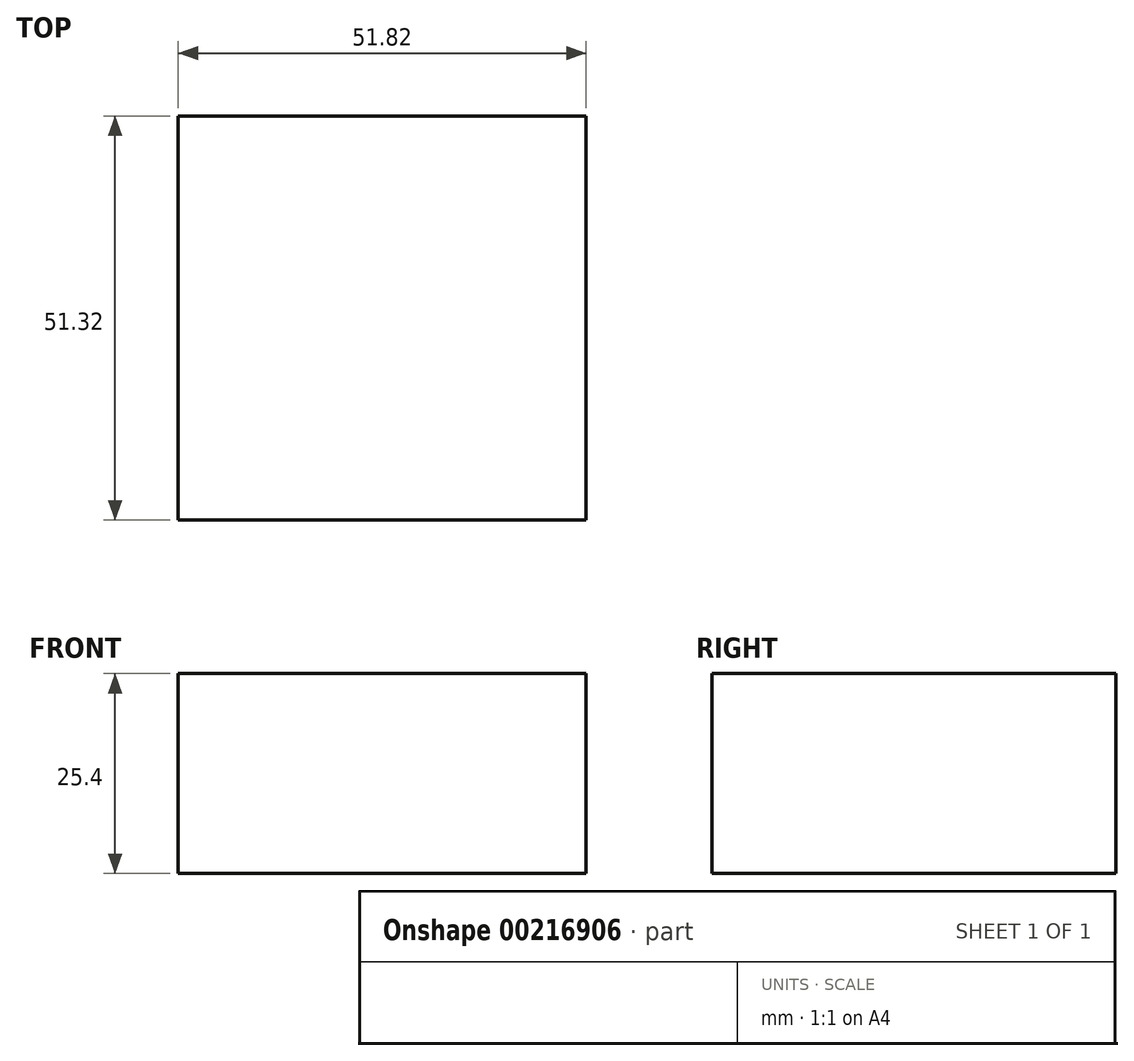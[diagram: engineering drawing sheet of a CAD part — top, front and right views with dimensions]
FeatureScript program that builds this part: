
annotation { "Feature Type Name" : "Feature", "Feature Type Description" : "" }
export const myFeature = defineFeature(function(context is Context, id is Id, definition is map)
    precondition{}
    {
        {
            var Q0;
            Q0=qCreatedBy(makeId("Top.planeOp"),FACE);
            var sketch = newSketch(context, id + "F0", { "sketchPlane" : qUnion([Q0])});
            skLineSegment(sketch, "E0", {"start": v(0, 0) * mm, "end": v(0, 51.32) * mm});
            skLineSegment(sketch, "E1", {"start": v(0, 51.32) * mm, "end": v(51.82, 51.32) * mm});
            skLineSegment(sketch, "E2", {"start": v(51.82, 51.32) * mm, "end": v(51.82, 0) * mm});
            skLineSegment(sketch, "E3", {"start": v(51.82, 0) * mm, "end": v(0, 0) * mm});
            skLineSegment(sketch, "E4.bottom", {"start": v(-45.17, 23.35) * mm, "end": v(-10.5, 23.35) * mm});
            skLineSegment(sketch, "E4.top", {"start": v(-45.17, -12.67) * mm, "end": v(-10.5, -12.67) * mm});
            skLineSegment(sketch, "E4.left", {"start": v(-45.17, 23.35) * mm, "end": v(-45.17, -12.67) * mm});
            skLineSegment(sketch, "E4.right", {"start": v(-10.5, 23.35) * mm, "end": v(-10.5, -12.67) * mm});
            skLineSegment(sketch, "E5.bottom", {"start": v(-10.5, -12.67) * mm, "end": v(12.96, -12.67) * mm});
            skLineSegment(sketch, "E5.top", {"start": v(-10.5, -59.16) * mm, "end": v(12.96, -59.16) * mm});
            skLineSegment(sketch, "E5.left", {"start": v(-10.5, -12.67) * mm, "end": v(-10.5, -59.16) * mm});
            skLineSegment(sketch, "E5.right", {"start": v(12.96, -12.67) * mm, "end": v(12.96, -59.16) * mm});
            skLineSegment(sketch, "E6.bottom", {"start": v(-10.5, 23.35) * mm, "end": v(-42.75, 23.35) * mm});
            skLineSegment(sketch, "E6.top", {"start": v(-10.5, 56.42) * mm, "end": v(-42.75, 56.42) * mm});
            skLineSegment(sketch, "E6.left", {"start": v(-10.5, 23.35) * mm, "end": v(-10.5, 56.42) * mm});
            skLineSegment(sketch, "E6.right", {"start": v(-42.75, 23.35) * mm, "end": v(-42.75, 56.42) * mm});
            skLineSegment(sketch, "E7.bottom", {"start": v(-45.17, -12.67) * mm, "end": v(-59.37, -12.67) * mm});
            skLineSegment(sketch, "E7.top", {"start": v(-45.17, -44.72) * mm, "end": v(-59.37, -44.72) * mm});
            skLineSegment(sketch, "E7.left", {"start": v(-45.17, -12.67) * mm, "end": v(-45.17, -44.72) * mm});
            skLineSegment(sketch, "E7.right", {"start": v(-59.37, -12.67) * mm, "end": v(-59.37, -44.72) * mm});
            skSolve(sketch);
        }
        {
            var Q0;
            Q0=makeQuery(id+"F0.imprint","IMPRINT",FACE,{"disambiguationData":[TD([[makeQuery(id+"F0.imprint","IMPRINT",EDGE,{"derivedFrom":sQuery(id+"F0.wireOp",EDGE,"E0")}),-1.0]])]});
            extrude(context, id + "F1", {"entities" : qUnion([Q0]), "depth" : 25.4 * mm});
        }
    });
